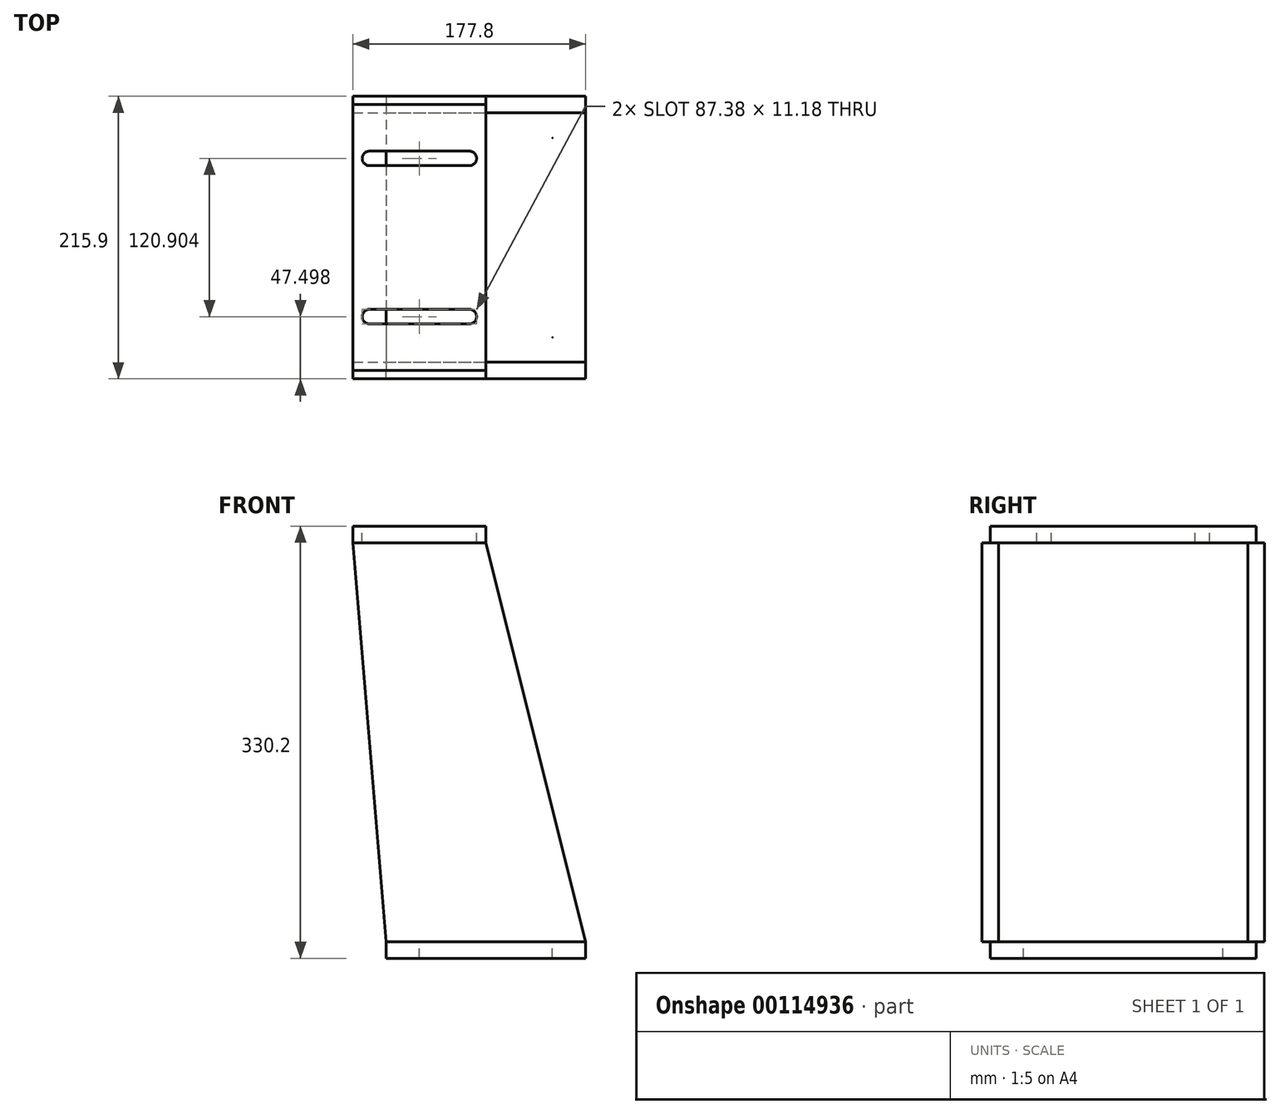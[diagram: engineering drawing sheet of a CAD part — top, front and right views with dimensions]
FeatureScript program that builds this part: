
annotation { "Feature Type Name" : "Feature", "Feature Type Description" : "" }
export const myFeature = defineFeature(function(context is Context, id is Id, definition is map)
    precondition{}
    {
        {
            var Q0;
            Q0=qCreatedBy(makeId("Top.planeOp"),FACE);
            cPlane(context, id + "F0", {"entities" : qUnion([Q0]), "cplaneType" : CPlaneType.OFFSET, "offset" : 330.2 * mm, "width" : 152.4 * mm, "height" : 152.4 * mm});
        }
        {
            var Q0;
            Q0=qCreatedBy(id+"F0.planeOp",FACE);
            var sketch = newSketch(context, id + "F1", { "sketchPlane" : qUnion([Q0])});
            skLineSegment(sketch, "E0.bottom", {"start": v(-50.8, 101.6) * mm, "end": v(50.8, 101.6) * mm});
            skLineSegment(sketch, "E0.top", {"start": v(-50.8, -101.6) * mm, "end": v(50.8, -101.6) * mm});
            skLineSegment(sketch, "E0.left", {"start": v(-50.8, 101.6) * mm, "end": v(-50.8, -101.6) * mm});
            skLineSegment(sketch, "E0.right", {"start": v(50.8, 101.6) * mm, "end": v(50.8, -101.6) * mm});
            skPoint(sketch, "E0.middle", {"position": v(0, 0) * mm});
            skLineSegment(sketch, "E1", {"start": v(-92.36, 0) * mm, "end": v(100.88, 0) * mm, "construction": true});
            skLineSegment(sketch, "E2", {"start": v(0, 138.54) * mm, "end": v(0, -143.13) * mm, "construction": true});
            skPoint(sketch, "E2.endSnap0", {"position": v(0, -101.6) * mm});
            skLineSegment(sketch, "E3.0", {"start": v(-38.1, 60.45) * mm, "end": v(38.1, 60.45) * mm});
            skLineSegment(sketch, "E4.0", {"start": v(-38.1, 138.54) * mm, "end": v(-38.1, -143.13) * mm, "construction": true});
            skLineSegment(sketch, "E5.MirrorCS", {"start": v(38.1, 138.54) * mm, "end": v(38.1, -143.13) * mm, "construction": true});
            skArc(sketch, "E6.0.startCap", {"start": v(-38.1, 54.86) * mm, "mid": v(-43.69, 60.45) * mm, "end": v(-38.1, 66.04) * mm});
            skArc(sketch, "E6.0.endCap", {"start": v(38.1, 66.04) * mm, "mid": v(43.69, 60.45) * mm, "end": v(38.1, 54.86) * mm});
            skLineSegment(sketch, "E6.0.left", {"start": v(-38.1, 66.04) * mm, "end": v(38.1, 66.04) * mm});
            skLineSegment(sketch, "E6.0.right", {"start": v(-38.1, 54.86) * mm, "end": v(38.1, 54.86) * mm});
            skLineSegment(sketch, "E7.MirrorCS", {"start": v(-38.1, -54.86) * mm, "end": v(38.1, -54.86) * mm});
            skLineSegment(sketch, "E8.MirrorCS", {"start": v(-38.1, -66.04) * mm, "end": v(38.1, -66.04) * mm});
            skArc(sketch, "E9.MirrorCS", {"start": v(38.1, -66.04) * mm, "mid": v(43.69, -60.45) * mm, "end": v(38.1, -54.86) * mm});
            skArc(sketch, "E10.MirrorCS", {"start": v(-38.1, -54.86) * mm, "mid": v(-43.69, -60.45) * mm, "end": v(-38.1, -66.04) * mm});
            skLineSegment(sketch, "E11.MirrorCS", {"start": v(-38.1, -60.45) * mm, "end": v(38.1, -60.45) * mm});
            skSolve(sketch);
        }
        {
            var Q0;
            Q0 = qSketchRegion(id + "F1", true);
            extrude(context, id + "F2", {"entities" : qUnion([Q0]), "oppositeDirection" : true, "depth" : 12.7 * mm});
        }
        {
            var Q0;
            Q0=qCreatedBy(makeId("Top.planeOp"),FACE);
            var sketch = newSketch(context, id + "F3", { "sketchPlane" : qUnion([Q0])});
            skLineSegment(sketch, "E12.0", {"start": v(-50.8, 101.6) * mm, "end": v(-50.8, -101.6) * mm, "construction": true});
            skLineSegment(sketch, "E13.0", {"start": v(-25.4, 101.6) * mm, "end": v(-25.4, -101.6) * mm});
            skLineSegment(sketch, "E14.0", {"start": v(127, 101.6) * mm, "end": v(127, -101.6) * mm});
            skLineSegment(sketch, "E15", {"start": v(-25.4, 101.6) * mm, "end": v(127, 101.6) * mm});
            skLineSegment(sketch, "E16", {"start": v(-25.4, -101.6) * mm, "end": v(127, -101.6) * mm});
            skSolve(sketch);
        }
        {
            var Q0;
            Q0 = qSketchRegion(id + "F3", true);
            extrude(context, id + "F4", {"entities" : qUnion([Q0]), "depth" : 12.7 * mm});
        }
        {
            var Q0;
            Q0=makeQuery(id+"F4.opExtrude","CAP_FACE",FACE,{"disambiguationData":[OSD([sQuery(id+"F3.wireOp",EDGE,"E13.0"),sQuery(id+"F3.wireOp",EDGE,"E14.0"),sQuery(id+"F3.wireOp",EDGE,"E15"),sQuery(id+"F3.wireOp",EDGE,"E16")])],"isStart":false});
            var sketch = newSketch(context, id + "F5", { "sketchPlane" : qUnion([Q0])});
            skLineSegment(sketch, "E17", {"start": v(50.8, 101.6) * mm, "end": v(50.8, -101.6) * mm, "construction": true});
            skLineSegment(sketch, "E18", {"start": v(127, 0) * mm, "end": v(-25.4, 0) * mm, "construction": true});
            skLineSegment(sketch, "E19.0", {"start": v(127, 76.2) * mm, "end": v(-25.4, 76.2) * mm, "construction": true});
            skLineSegment(sketch, "E20.0", {"start": v(0, 101.6) * mm, "end": v(0, -101.6) * mm, "construction": true});
            skPoint(sketch, "E21", {"position": v(0, 76.2) * mm});
            skPoint(sketch, "E22.MirrorP", {"position": v(101.6, 76.2) * mm});
            skPoint(sketch, "E23.MirrorP", {"position": v(101.6, -76.2) * mm});
            skPoint(sketch, "E24.MirrorP", {"position": v(0, -76.2) * mm});
            skSolve(sketch);
        }
        {
            var Q0;
            Q0=sQuery(id+"F5.wireOp",VERTEX,"E21");
            var Q1;
            Q1=sQuery(id+"F5.wireOp",VERTEX,"E22.MirrorP");
            var Q2;
            Q2=sQuery(id+"F5.wireOp",VERTEX,"E24.MirrorP");
            var Q3;
            Q3=sQuery(id+"F5.wireOp",VERTEX,"E23.MirrorP");
            var Q4;
            Q4=makeQuery(id+"F4.opExtrude","SWEPT_BODY",BODY,{"disambiguationData":[OSD([sQuery(id+"F3.wireOp",EDGE,"E13.0"),sQuery(id+"F3.wireOp",EDGE,"E14.0"),sQuery(id+"F3.wireOp",EDGE,"E15"),sQuery(id+"F3.wireOp",EDGE,"E16")])]});
            hole(context, id + "F6", {"style" : HoleStyle.SIMPLE, "endStyle" : HoleEndStyle.BLIND, "standardTappedOrClearance" : lookupTablePath({ "standard" : "ANSI", "size" : "9/16 (0.56)", "type" : "Drilled" }), "standardBlindInLast" : lookupTablePath({ "standard" : "ANSI", "size" : "9/16", "type" : "Drilled" }), "holeDiameter" : 9 / 406.4 * mm, "holeDepth" : 50.8 * mm, "locations" : qUnion([Q0, Q1, Q2, Q3]), "scope" : qUnion([Q4])});
        }
        {
            var Q0;
            Q0=makeQuery(id+"F2.opExtrude","SWEPT_FACE",FACE,{"disambiguationData":[OSD([sQuery(id+"F1.wireOp",EDGE,"E0.top")])]});
            var sketch = newSketch(context, id + "F7", { "sketchPlane" : qUnion([Q0])});
            skLineSegment(sketch, "E25.0", {"start": v(-50.8, 317.5) * mm, "end": v(50.8, 317.5) * mm});
            skLineSegment(sketch, "E26.0", {"start": v(-25.4, 12.7) * mm, "end": v(127, 12.7) * mm});
            skLineSegment(sketch, "E27", {"start": v(-50.8, 317.5) * mm, "end": v(-25.4, 12.7) * mm});
            skLineSegment(sketch, "E28", {"start": v(50.8, 317.5) * mm, "end": v(127, 12.7) * mm});
            skSolve(sketch);
        }
        {
            var Q0;
            Q0=makeQuery(id+"F7.imprint","IMPRINT",FACE,{"disambiguationData":[TD([[makeQuery(id+"F7.imprint","IMPRINT",EDGE,{"derivedFrom":sQuery(id+"F7.wireOp",EDGE,"E25.0")}),-1.0]])]});
            extrude(context, id + "F8", {"entities" : qUnion([Q0]), "endBound" : BoundingType.SYMMETRIC, "depth" : 12.7 * mm});
        }
        {
            var Q0;
            Q0=makeQuery(id+"F8.opExtrude","SWEPT_BODY",BODY,{"disambiguationData":[OSD([sQuery(id+"F7.wireOp",EDGE,"E25.0"),sQuery(id+"F7.wireOp",EDGE,"E26.0"),sQuery(id+"F7.wireOp",EDGE,"E27"),sQuery(id+"F7.wireOp",EDGE,"E28")])]});
            var Q1;
            Q1=qCreatedBy(makeId("Front.planeOp"),FACE);
            mirror(context, id + "F9", {"entities" : qUnion([Q0]), "mirrorPlane" : qUnion([Q1])});
        }
    });
